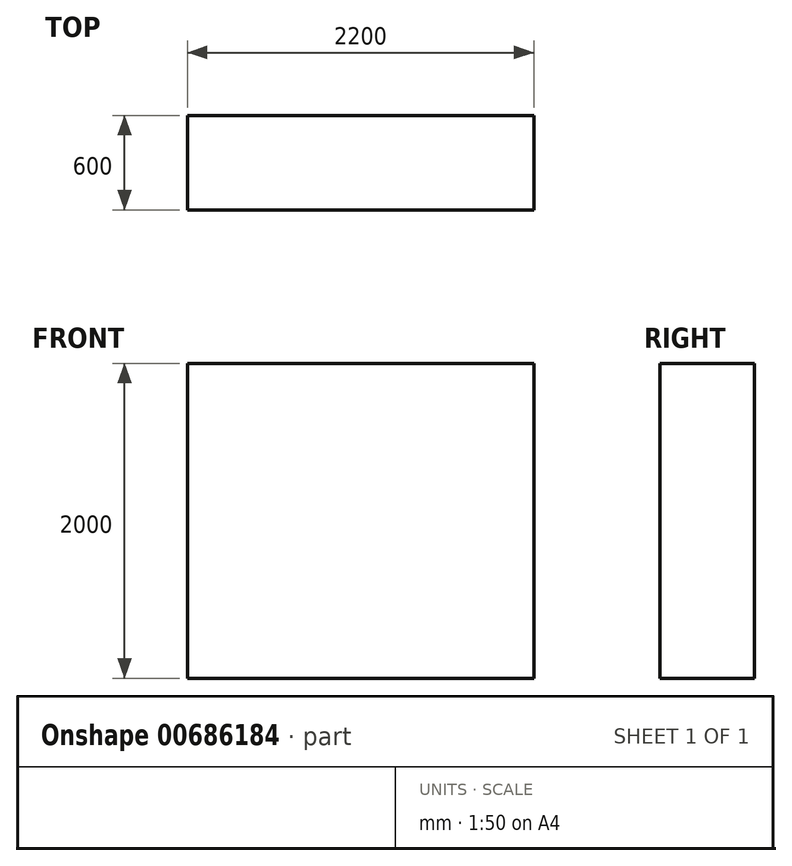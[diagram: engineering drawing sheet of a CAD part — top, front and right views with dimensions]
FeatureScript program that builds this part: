
annotation { "Feature Type Name" : "Feature", "Feature Type Description" : "" }
export const myFeature = defineFeature(function(context is Context, id is Id, definition is map)
    precondition{}
    {
        {
            var Q0;
            Q0=qCreatedBy(makeId("Top.planeOp"),FACE);
            var sketch = newSketch(context, id + "F0", { "sketchPlane" : qUnion([Q0])});
            skLineSegment(sketch, "E0.bottom", {"start": v(0, 0) * mm, "end": v(2200, 0) * mm});
            skLineSegment(sketch, "E0.top", {"start": v(0, -600) * mm, "end": v(2200, -600) * mm});
            skLineSegment(sketch, "E0.left", {"start": v(0, 0) * mm, "end": v(0, -600) * mm});
            skLineSegment(sketch, "E0.right", {"start": v(2200, 0) * mm, "end": v(2200, -600) * mm});
            skSolve(sketch);
        }
        {
            var Q0;
            Q0=makeQuery(id+"F0.imprint","IMPRINT",FACE,{"disambiguationData":[TD([[makeQuery(id+"F0.imprint","IMPRINT",EDGE,{"derivedFrom":sQuery(id+"F0.wireOp",EDGE,"E0.bottom")}),-1.0]])]});
            extrude(context, id + "F1", {"entities" : qUnion([Q0]), "depth" : 2000 * mm, "offsetDistance" : 25 * mm});
        }
    });
